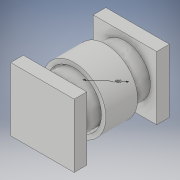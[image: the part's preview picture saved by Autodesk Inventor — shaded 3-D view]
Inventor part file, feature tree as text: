
AUTODESK INVENTOR PART (.ipt)
format: ipt  version: 2018 (Build 220112000, 112)  size: 131,072 bytes
history: native  units: in
note: dims shown in document units (in); Inventor stores cm internally (conversion verified against a paired STEP export)
features: extrude x4, sketch x3, plane x2, mirror x1
ambient origin geometry x8: Origin, YZ Plane, XZ Plane, XY Plane, X Axis, Y Axis, Z Axis, Center Point
bodies: Solid1 (feature_tree)
feature tree (10):
  sketch  "Sketch1"  dims[d0=0.4in d1=0.4in d2=0.0in]
  extrude  "Extrusion1"  Depth=0.4in TaperAngle=0.0deg
  plane  "Work Plane1"
  extrude  "Extrusion4"  Depth=0.5in
  extrude  "Extrusion5"  Depth=0.15in TaperAngle=0.0deg
  extrude  "Extrusion6"  Depth=0.5in
  plane  "Work Plane2"
  mirror  "Mirror1"
  sketch  "Sketch4"  dims[d13=0.43in d14=0.5in]
  sketch  "Sketch5"  dims[d15=0.25in d16=0.0in d17=0.15in d18=0.0in d19=0.5in d20=0.5in d21=0.25in d22=0.25in d23=0.1in d24=0.0in]
